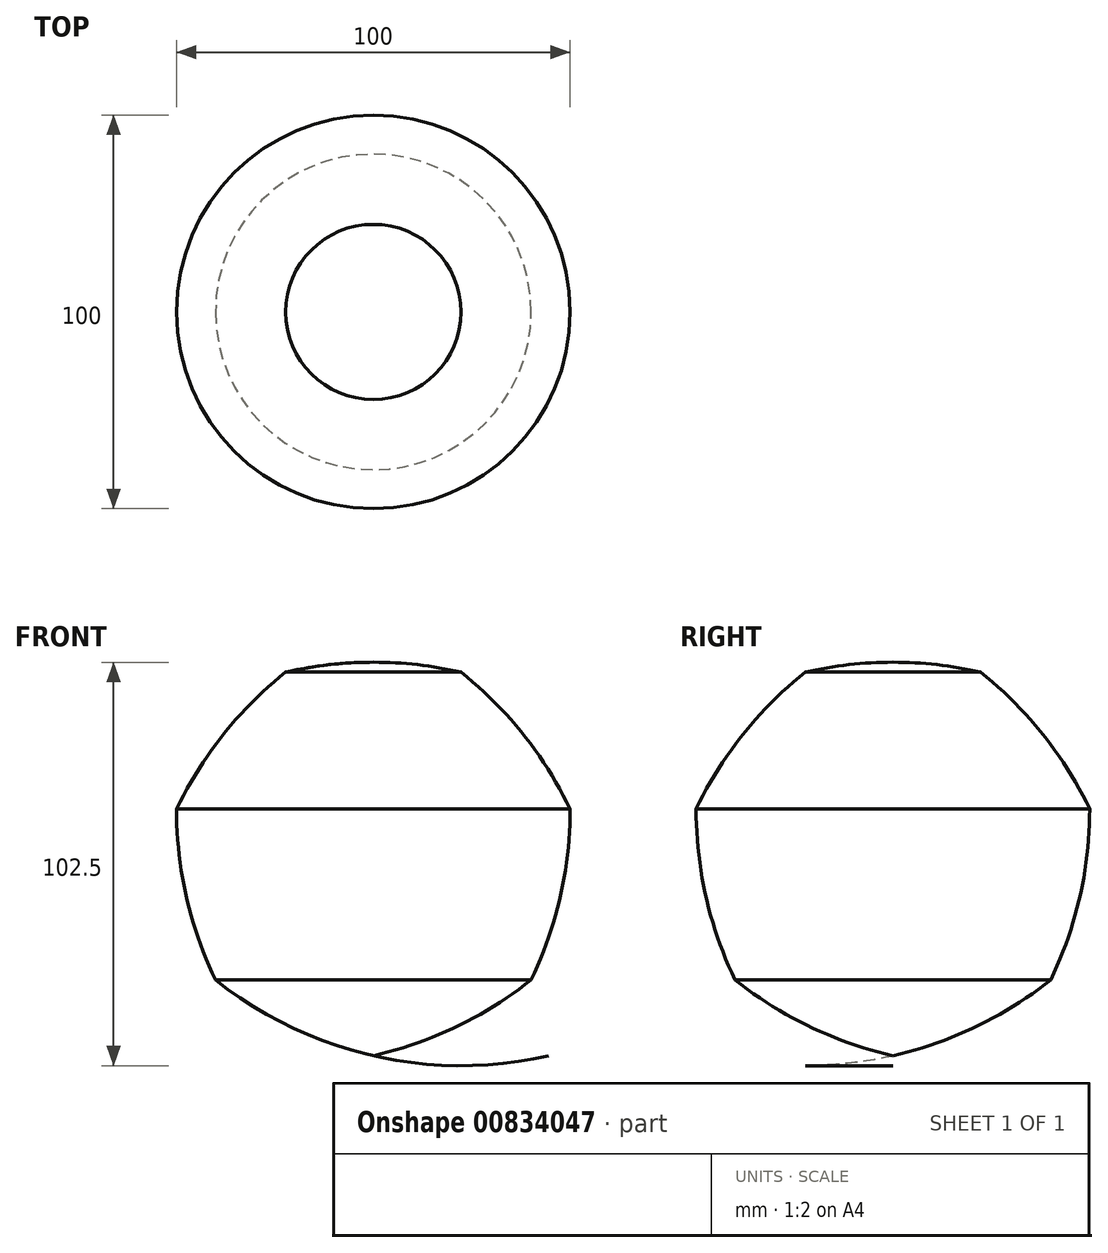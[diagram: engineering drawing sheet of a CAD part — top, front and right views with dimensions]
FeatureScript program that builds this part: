
annotation { "Feature Type Name" : "Feature", "Feature Type Description" : "" }
export const myFeature = defineFeature(function(context is Context, id is Id, definition is map)
    precondition{}
    {
        {
            var Q0;
            Q0=qCreatedBy(makeId("Front.planeOp"),FACE);
            var sketch = newSketch(context, id + "F0", { "sketchPlane" : qUnion([Q0])});
            skLineSegment(sketch, "E0.0", {"start": v(-22.25, 46.2) * mm, "end": v(22.25, 46.2) * mm, "construction": true});
            skLineSegment(sketch, "E0.1", {"start": v(22.25, 46.2) * mm, "end": v(50, 11.41) * mm, "construction": true});
            skLineSegment(sketch, "E0.2", {"start": v(50, 11.41) * mm, "end": v(40.1, -31.98) * mm, "construction": true});
            skLineSegment(sketch, "E0.3", {"start": v(40.1, -31.98) * mm, "end": v(0, -51.29) * mm, "construction": true});
            skLineSegment(sketch, "E0.4", {"start": v(0, -51.29) * mm, "end": v(-40.1, -31.98) * mm, "construction": true});
            skLineSegment(sketch, "E0.5", {"start": v(-40.1, -31.98) * mm, "end": v(-50, 11.41) * mm, "construction": true});
            skLineSegment(sketch, "E0.6", {"start": v(-50, 11.41) * mm, "end": v(-22.25, 46.2) * mm, "construction": true});
            skPoint(sketch, "E0.0.midPoint", {"position": v(0, 46.2) * mm});
            skArc(sketch, "E1", {"start": v(22.25, 46.2) * mm, "mid": v(0, 48.71) * mm, "end": v(-22.25, 46.2) * mm});
            skPoint(sketch, "E2", {"position": v(0, 48.71) * mm});
            skArc(sketch, "E3", {"start": v(50, 11.41) * mm, "mid": v(38.09, 30.37) * mm, "end": v(22.25, 46.2) * mm});
            skArc(sketch, "E4", {"start": v(40.1, -31.98) * mm, "mid": v(47.5, -10.84) * mm, "end": v(50, 11.41) * mm});
            skArc(sketch, "E5", {"start": v(-22.25, 46.2) * mm, "mid": v(-38.09, 30.37) * mm, "end": v(-50, 11.41) * mm});
            skArc(sketch, "E6", {"start": v(-50, 11.41) * mm, "mid": v(-47.5, -10.84) * mm, "end": v(-40.1, -31.98) * mm});
            skArc(sketch, "E7", {"start": v(-40.1, -31.98) * mm, "mid": v(-21.14, -43.89) * mm, "end": v(0, -51.29) * mm});
            skArc(sketch, "E8", {"start": v(0, -51.29) * mm, "mid": v(21.14, -43.89) * mm, "end": v(40.1, -31.98) * mm});
            skLineSegment(sketch, "E9", {"start": v(0, 48.71) * mm, "end": v(0, -51.29) * mm});
            skSolve(sketch);
        }
        {
            var Q0;
            {var subQ0=sQuery(id+"F0.wireOp",EDGE,"E5");Q0=makeQuery(id+"F0.imprint","IMPRINT",FACE,{"disambiguationData":[TD([[makeQuery(id+"F0.imprint","IMPRINT",EDGE,{"derivedFrom":subQ0}),1.0]])]});}
            var Q1;
            Q1=sQuery(id+"F0.wireOp",EDGE,"E9");
            revolve(context, id + "F1", {"surfaceOperationType" : NewSurfaceOperationType.NEW, "entities" : qUnion([Q0]), "axis" : qUnion([Q1]), "revolveType" : RevolveType.FULL});
        }
    });
